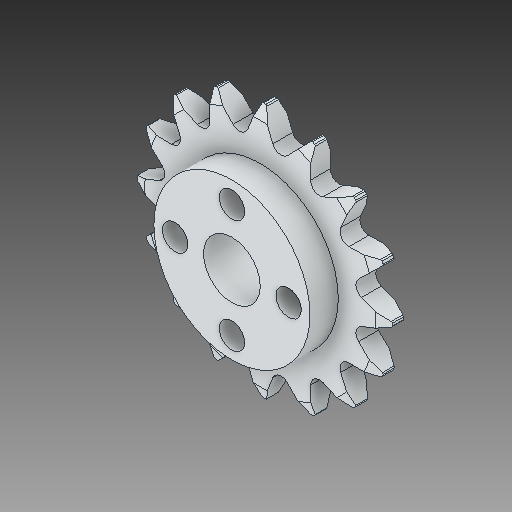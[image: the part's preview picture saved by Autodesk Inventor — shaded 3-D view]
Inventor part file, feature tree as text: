
AUTODESK INVENTOR PART (.ipt)
format: ipt  version: 2018.3 (Build 223284000, 284)  size: 354,304 bytes
history: native  units: mm
features: extrude x1
ambient origin geometry x8: Origin, YZ Plane, XZ Plane, XY Plane, X Axis, Y Axis, Z Axis, Center Point
bodies: Solid1 (feature_tree)
feature tree (1):
  extrude  "Extrude6"  [1 undecoded]
note: 1 required parameter value undecoded (feature->parameter linkage not recoverable at this tier; creation-order binding heuristic only, values carry confidence <= 0.55)
